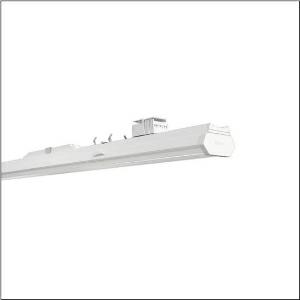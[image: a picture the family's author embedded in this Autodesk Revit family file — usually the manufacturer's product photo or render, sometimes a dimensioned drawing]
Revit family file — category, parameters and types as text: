
# Revit family: licross_r__11_protected_extreme_mo_51tp11dn49xfe_238d
name_source: partatom
category: Lighting Fixtures
units: mm (PartAtom-declared; Revit-internal decimal feet)

## family parameters
Cut with Voids When Loaded = No
Host = Face
Light Source = No
Part Type = Normal
Room Calculation Point = No
Round Connector Dimension = Use Diameter
Shared = No

## types (1)
- --- (1 x LED, 9080 lm, 56.9 W, 4000K)
    Apparent Load = 57 VA
    CIE Flux Codes = 83 94 98 100 100
    Color Rendering = 80
    Color Temperature = 4000K
    Default Elevation = 1800 mm
    Description = Licross® 11 Protected extreme MOluminaire insert, length: 1.500mm, width: 90mm, height: 101mm, LED rated luminous flux: 9.080lm, light colour: 840, control gear: DALI 2, control gear: ECG DALI, with plug, 5-pole, with phase selection, mains connection: 220..240V, AC, 50/60Hz, halogen-free wiring, primary optical cover: cover, of PMMA, light emission: direct with ceiling illumination distribution, protection rating (complete): IP64, insulation class (complete): insulation class I (protective earthing), certification: CE, ENEC, VDE, protection symbol: D if used in an environment with conductive dust loads with corresponding accessories, permissible ambient temperature for indoor applications: -25..+50°C, reducing of maximum allowable ambient temperature of 5°C with ceiling mounting, corresponds to IFS (International Featured Standards) requirements for safety and quality in the food industry, packaging unit: 1 piece
    Height = 92 mm
    Lamp = 1 x LED
    Lamp Light Flux = 9080 lm
    Lamp Power = 56.9 W
    Lamp count = 1
    Length = 1500 mm
    Luminous efficacy = 160 lm/W
    Manufacturer = Siteco
    ModVariant = No
    Model = 51TP11DN49XFE
    Mounting Place = Ceiling
    Mounting Type = Pendant
    Number of Poles = 1
    OnlyDefault = Yes
    Power Factor = 1
    Product Name = Licross® 11 Protected extreme MO
    Product group = luminaire insert
    ProductGroupID = 902
    Protection Class = Protection class I
    Protection Degree = IP 64
    RLX_Detail_Level = 1
    RlxData = <blob elided: 23769 chars, md5=30d3c254>
    Socket = socket
    Standby Power = 0 W
    System Light Flux = 9080 lm
    System Power = 57 W
    Type Comments = factory setting: luminous flux: 100 % | dim-lin: 254 | 375 mA
    Type Image = l_1256148.jpg
    URL = http://relux.com
    VarID = @adj_132674
    Voltage = 0 V
    Weight = 0.00 kg
    Width = 88 mm

## geometry (parser evidence)
native form markers: Blend x4, Sweep x9
no freeform markers — native parametric forms only
